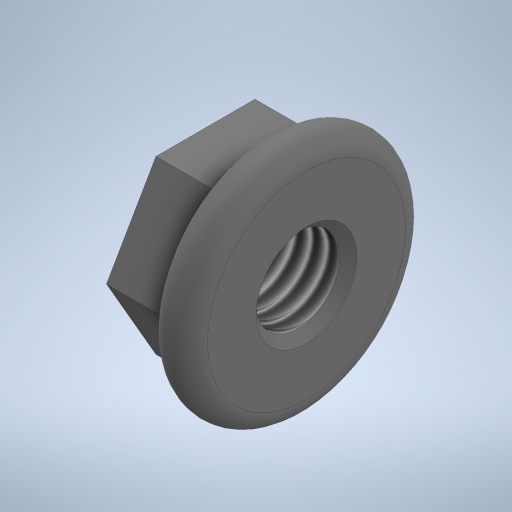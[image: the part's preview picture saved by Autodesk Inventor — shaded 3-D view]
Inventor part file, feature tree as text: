
AUTODESK INVENTOR PART (.ipt)
format: ipt  version: 2024 (Build 280153000, 153)  size: 302,592 bytes
history: native  units: in
note: dims shown in document units (in); Inventor stores cm internally (conversion verified against a paired STEP export)
features: sketch x3, extrude x2, revolve x1, plane x1, chamfer x1, thread x1, direct_edit x1, other x1
ambient origin geometry x8: Origin, YZ Plane, XZ Plane, XY Plane, X Axis, Y Axis, Z Axis, Center Point
bodies: Solid1 (feature_tree)
feature tree (11):
  revolve  "Revolution1"  Angle=90.0deg
  plane  "Work Plane1"
  sketch  "Sketch2"  dims[d7=0.0in d8=0.3858in]
  sketch  "Sketch3"  dims[d9=0.1628in d10=0.1969in d11=0.0in d12=0.1969in d13=0.0in d14=0.017in d15=0.0787in d16=45.0deg d17=0.2362in d18=0.0in d19=3.937in d20=0.3937in d21=0.3937in]
  extrude  "Extrusion1"  Depth=0.3858in
  extrude  "Extrusion2"  Depth=0.3937in TaperAngle=0.0deg
  chamfer  "Chamfer1"  Distance=0.1969in
  thread  "Thread1"  [1 undecoded]
  direct_edit  "Direct Edit1"
  sketch  "Sketch1"  dims[d4=0.0394in d6=90.0deg]
  other  "Scale1"
note: 1 required parameter value undecoded (feature->parameter linkage not recoverable at this tier; creation-order binding heuristic only, values carry confidence <= 0.55)
